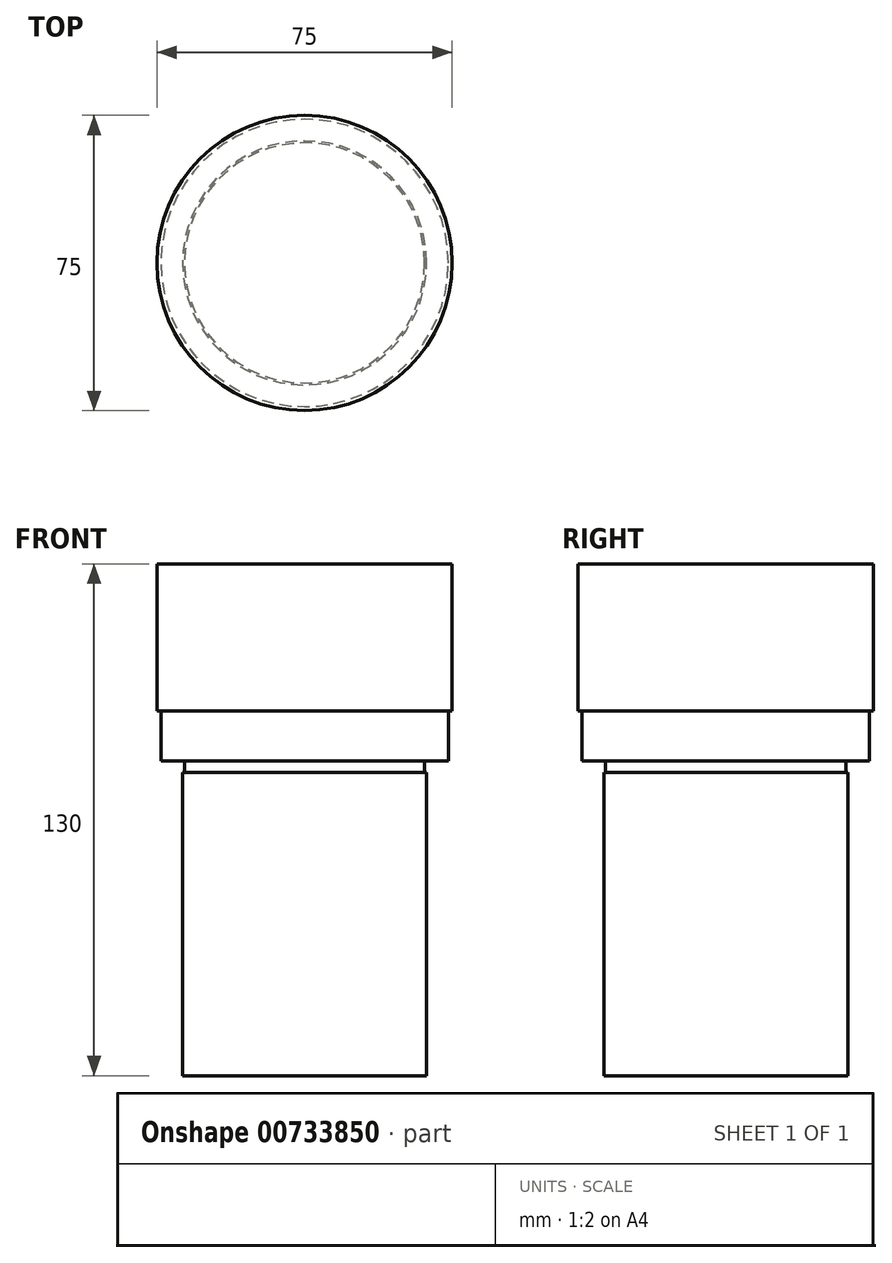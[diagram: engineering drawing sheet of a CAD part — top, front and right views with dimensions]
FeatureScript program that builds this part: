
annotation { "Feature Type Name" : "Feature", "Feature Type Description" : "" }
export const myFeature = defineFeature(function(context is Context, id is Id, definition is map)
    precondition{}
    {
        {
            var Q0;
            Q0=qCreatedBy(makeId("Front.planeOp"),FACE);
            var sketch = newSketch(context, id + "F0", { "sketchPlane" : qUnion([Q0])});
            skLineSegment(sketch, "E0", {"start": v(0, 0) * mm, "end": v(-31, 0) * mm});
            skLineSegment(sketch, "E1", {"start": v(-31, 0) * mm, "end": v(-31, 77) * mm});
            skLineSegment(sketch, "E2", {"start": v(-31, 77) * mm, "end": v(-30.5, 77) * mm});
            skLineSegment(sketch, "E3", {"start": v(-30.5, 77) * mm, "end": v(-30.5, 80) * mm});
            skLineSegment(sketch, "E4", {"start": v(-30.5, 80) * mm, "end": v(-36.5, 80) * mm});
            skLineSegment(sketch, "E5", {"start": v(-36.5, 80) * mm, "end": v(-36.5, 92.7) * mm});
            skLineSegment(sketch, "E6", {"start": v(-36.5, 92.7) * mm, "end": v(-37.5, 92.7) * mm});
            skLineSegment(sketch, "E7", {"start": v(-37.5, 92.7) * mm, "end": v(-37.5, 130) * mm});
            skLineSegment(sketch, "E8", {"start": v(-37.5, 130) * mm, "end": v(0, 130) * mm});
            skLineSegment(sketch, "E9", {"start": v(0, 130) * mm, "end": v(0, 0) * mm});
            skSolve(sketch);
        }
        {
            var Q0;
            Q0=makeQuery(id+"F0.imprint","IMPRINT",FACE,{"disambiguationData":[TD([[makeQuery(id+"F0.imprint","IMPRINT",EDGE,{"derivedFrom":sQuery(id+"F0.wireOp",EDGE,"E0")}),-1.0]])]});
            var Q1;
            Q1=sQuery(id+"F0.wireOp",EDGE,"E9");
            revolve(context, id + "F1", {"surfaceOperationType" : NewSurfaceOperationType.NEW, "entities" : qUnion([Q0]), "axis" : qUnion([Q1]), "revolveType" : RevolveType.FULL});
        }
    });
